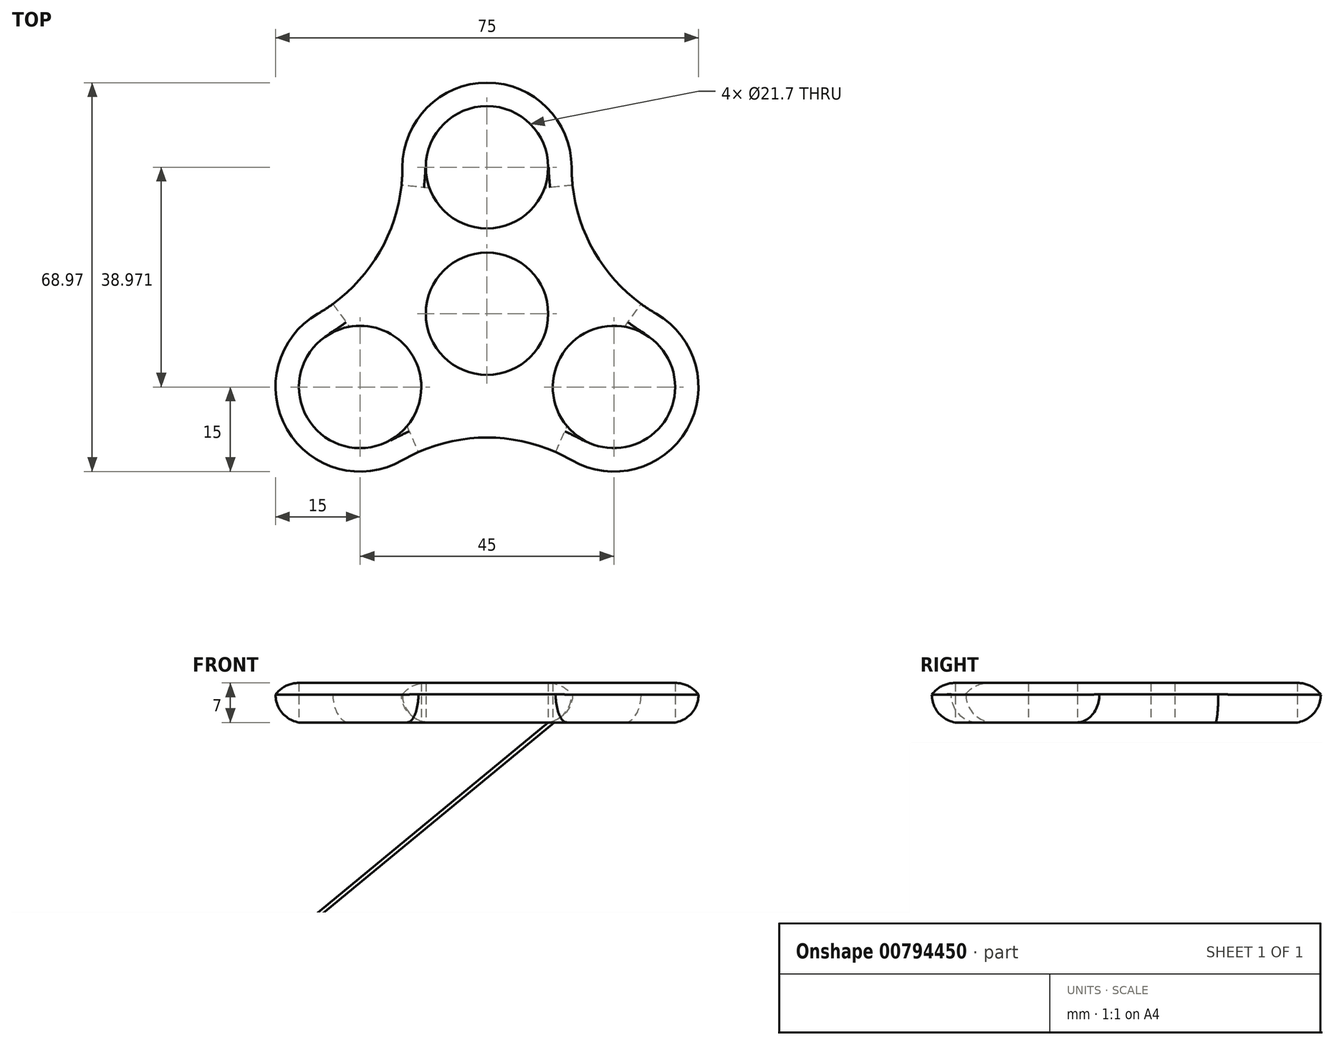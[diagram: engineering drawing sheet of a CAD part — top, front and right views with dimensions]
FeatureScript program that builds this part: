
annotation { "Feature Type Name" : "Feature", "Feature Type Description" : "" }
export const myFeature = defineFeature(function(context is Context, id is Id, definition is map)
    precondition{}
    {
        {
            var Q0;
            Q0=qCreatedBy(makeId("Top.planeOp"),FACE);
            var sketch = newSketch(context, id + "F0", { "sketchPlane" : qUnion([Q0])});
            skLineSegment(sketch, "E0", {"start": v(0, 38.97) * mm, "end": v(-22.5, 0) * mm, "construction": true});
            skLineSegment(sketch, "E1", {"start": v(-22.5, 0) * mm, "end": v(22.5, 0) * mm, "construction": true});
            skLineSegment(sketch, "E2", {"start": v(22.5, 0) * mm, "end": v(0, 38.97) * mm, "construction": true});
            skLineSegment(sketch, "E3", {"start": v(-22.5, 0) * mm, "end": v(-45, 38.97) * mm, "construction": true});
            skLineSegment(sketch, "E4", {"start": v(-45, 38.97) * mm, "end": v(0, 38.97) * mm, "construction": true});
            skLineSegment(sketch, "E5", {"start": v(0, 38.97) * mm, "end": v(45, 38.97) * mm, "construction": true});
            skLineSegment(sketch, "E6", {"start": v(45, 38.97) * mm, "end": v(22.5, 0) * mm, "construction": true});
            skLineSegment(sketch, "E7", {"start": v(22.5, 0) * mm, "end": v(0, -38.97) * mm, "construction": true});
            skLineSegment(sketch, "E8", {"start": v(0, -38.97) * mm, "end": v(-22.5, 0) * mm, "construction": true});
            skArc(sketch, "E9", {"start": v(15, 38.97) * mm, "mid": v(0, 53.97) * mm, "end": v(-15, 38.97) * mm});
            skArc(sketch, "E10", {"start": v(-30, 13) * mm, "mid": v(-35.5, -7.5) * mm, "end": v(-15, -13) * mm});
            skArc(sketch, "E11", {"start": v(15, -13) * mm, "mid": v(35.5, -7.5) * mm, "end": v(30, 13) * mm});
            skArc(sketch, "E12", {"start": v(-30, 13) * mm, "mid": v(-19.02, 23.97) * mm, "end": v(-15, 38.97) * mm});
            skArc(sketch, "E13", {"start": v(15, -13) * mm, "mid": v(0, -8.97) * mm, "end": v(-15, -13) * mm});
            skArc(sketch, "E14", {"start": v(15, 38.97) * mm, "mid": v(19.02, 23.97) * mm, "end": v(30, 13) * mm});
            skLineSegment(sketch, "E15", {"start": v(-22.5, 0) * mm, "end": v(11.25, 19.49) * mm, "construction": true});
            skLineSegment(sketch, "E16", {"start": v(11.25, 19.49) * mm, "end": v(22.5, 0) * mm, "construction": true});
            skLineSegment(sketch, "E17", {"start": v(22.5, 0) * mm, "end": v(-11.25, 19.49) * mm, "construction": true});
            skLineSegment(sketch, "E18", {"start": v(-11.25, 19.49) * mm, "end": v(0, 38.97) * mm, "construction": true});
            skLineSegment(sketch, "E19", {"start": v(0, 38.97) * mm, "end": v(0, 0) * mm, "construction": true});
            skCircle(sketch, "E20", {"center": v(0, 13) * mm, "radius": 10.85 * mm});
            skCircle(sketch, "E21", {"center": v(22.5, 0) * mm, "radius": 10.85 * mm});
            skCircle(sketch, "E22", {"center": v(0, 38.97) * mm, "radius": 10.85 * mm});
            skCircle(sketch, "E23", {"center": v(-22.5, 0) * mm, "radius": 10.85 * mm});
            skSolve(sketch);
        }
        {
            var Q0;
            Q0=makeQuery(id+"F0.imprint","IMPRINT",FACE,{"disambiguationData":[TD([[makeQuery(id+"F0.imprint","IMPRINT",EDGE,{"derivedFrom":sQuery(id+"F0.wireOp",EDGE,"E9")}),1.0]])]});
            extrude(context, id + "F1", {"entities" : qUnion([Q0]), "depth" : 7 * mm, "offsetDistance" : 25 * mm});
        }
        {
            var Q0;
            Q0=makeQuery(id+"F1.opExtrude","CAP_EDGE",EDGE,{"disambiguationData":[OSD([sQuery(id+"F0.wireOp",EDGE,"E12")])],"isStart":true});
            var Q1;
            Q1=makeQuery(id+"F1.opExtrude","CAP_EDGE",EDGE,{"disambiguationData":[OSD([sQuery(id+"F0.wireOp",EDGE,"E10")])],"isStart":true});
            var Q2;
            Q2=makeQuery(id+"F1.opExtrude","CAP_EDGE",EDGE,{"disambiguationData":[OSD([sQuery(id+"F0.wireOp",EDGE,"E13")])],"isStart":true});
            var Q3;
            Q3=makeQuery(id+"F1.opExtrude","CAP_EDGE",EDGE,{"disambiguationData":[OSD([sQuery(id+"F0.wireOp",EDGE,"E14")])],"isStart":true});
            var Q4;
            Q4=makeQuery(id+"F1.opExtrude","CAP_EDGE",EDGE,{"disambiguationData":[OSD([sQuery(id+"F0.wireOp",EDGE,"E11")])],"isStart":true});
            var Q5;
            Q5=makeQuery(id+"F1.opExtrude","CAP_EDGE",EDGE,{"disambiguationData":[OSD([sQuery(id+"F0.wireOp",EDGE,"E9")])],"isStart":true});
            fillet(context, id + "F2", {"entities" : qUnion([Q0, Q1, Q2, Q3, Q4, Q5]), "radius" : 5 * mm, "tangentPropagation" : true, "allowEdgeOverflow" : false});
        }
        {
            var Q0;
            Q0=makeQuery(id+"F1.opExtrude","CAP_EDGE",EDGE,{"disambiguationData":[OSD([sQuery(id+"F0.wireOp",EDGE,"E9")])],"isStart":false});
            var Q1;
            Q1=makeQuery(id+"F1.opExtrude","CAP_EDGE",EDGE,{"disambiguationData":[OSD([sQuery(id+"F0.wireOp",EDGE,"E12")])],"isStart":false});
            var Q2;
            Q2=makeQuery(id+"F1.opExtrude","CAP_EDGE",EDGE,{"disambiguationData":[OSD([sQuery(id+"F0.wireOp",EDGE,"E10")])],"isStart":false});
            var Q3;
            Q3=makeQuery(id+"F1.opExtrude","CAP_EDGE",EDGE,{"disambiguationData":[OSD([sQuery(id+"F0.wireOp",EDGE,"E14")])],"isStart":false});
            var Q4;
            Q4=makeQuery(id+"F1.opExtrude","CAP_EDGE",EDGE,{"disambiguationData":[OSD([sQuery(id+"F0.wireOp",EDGE,"E11")])],"isStart":false});
            var Q5;
            Q5=makeQuery(id+"F1.opExtrude","CAP_EDGE",EDGE,{"disambiguationData":[OSD([sQuery(id+"F0.wireOp",EDGE,"E13")])],"isStart":false});
            fillet(context, id + "F3", {"entities" : qUnion([Q0, Q1, Q2, Q3, Q4, Q5]), "radius" : 5 * mm, "tangentPropagation" : true, "allowEdgeOverflow" : false});
        }
    });
